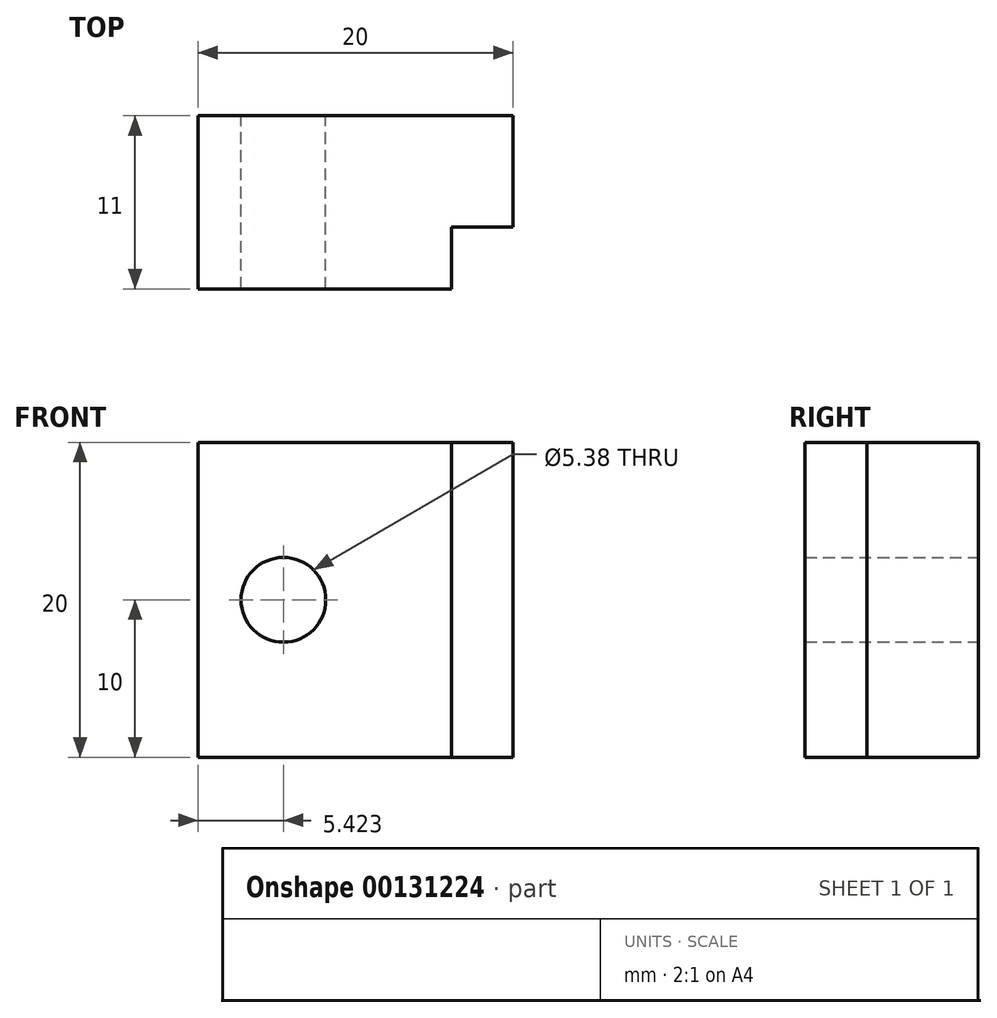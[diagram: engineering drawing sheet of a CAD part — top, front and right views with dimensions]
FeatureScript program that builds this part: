
annotation { "Feature Type Name" : "Feature", "Feature Type Description" : "" }
export const myFeature = defineFeature(function(context is Context, id is Id, definition is map)
    precondition{}
    {
        {
            var Q0;
            Q0=qCreatedBy(makeId("Front.planeOp"),FACE);
            var sketch = newSketch(context, id + "F0", { "sketchPlane" : qUnion([Q0])});
            skLineSegment(sketch, "E0.bottom", {"start": v(0, 0) * mm, "end": v(20, 0) * mm});
            skLineSegment(sketch, "E0.top", {"start": v(0, 20) * mm, "end": v(20, 20) * mm});
            skLineSegment(sketch, "E0.left", {"start": v(0, 0) * mm, "end": v(0, 20) * mm});
            skLineSegment(sketch, "E0.right", {"start": v(20, 0) * mm, "end": v(20, 20) * mm});
            skLineSegment(sketch, "E1", {"start": v(-7.51, 0) * mm, "end": v(-7.51, 10) * mm});
            skLineSegment(sketch, "E2", {"start": v(0, 10) * mm, "end": v(2.7, 10) * mm});
            skPoint(sketch, "E2.endSnap0", {"position": v(0, 10) * mm});
            skCircle(sketch, "E3", {"center": v(5.42, 10) * mm, "radius": 2.7 * mm});
            skSolve(sketch);
        }
        {
            var Q0;
            Q0=makeQuery(id+"F0.imprint","IMPRINT",FACE,{"disambiguationData":[TD([[makeQuery(id+"F0.imprint","IMPRINT",EDGE,{"derivedFrom":sQuery(id+"F0.wireOp",EDGE,"E0.bottom")}),1.0]])]});
            extrude(context, id + "F1", {"entities" : qUnion([Q0]), "depth" : 11 * mm});
        }
        {
            var Q0;
            Q0=qCreatedBy(makeId("Top.planeOp"),FACE);
            var sketch = newSketch(context, id + "F2", { "sketchPlane" : qUnion([Q0])});
            skLineSegment(sketch, "E4", {"start": v(20.56, -11.08) * mm, "end": v(20.56, -7.08) * mm});
            skLineSegment(sketch, "E5", {"start": v(20.09, -11.36) * mm, "end": v(16.09, -11.36) * mm});
            skLineSegment(sketch, "E6", {"start": v(16.09, -11.36) * mm, "end": v(6.09, -11.36) * mm});
            skLineSegment(sketch, "E7", {"start": v(0, 2.37) * mm, "end": v(6, 2.37) * mm});
            skLineSegment(sketch, "E8", {"start": v(6, 1.19) * mm, "end": v(3.3, 1.19) * mm});
            skLineSegment(sketch, "E9", {"start": v(6.09, -12.78) * mm, "end": v(8.79, -12.78) * mm});
            skLineSegment(sketch, "E10.bottom", {"start": v(20.09, -11.08) * mm, "end": v(16.09, -11.08) * mm});
            skLineSegment(sketch, "E10.top", {"start": v(20.09, -7.08) * mm, "end": v(16.09, -7.08) * mm});
            skLineSegment(sketch, "E10.left", {"start": v(20.09, -11.08) * mm, "end": v(20.09, -7.08) * mm});
            skLineSegment(sketch, "E10.right", {"start": v(16.09, -11.08) * mm, "end": v(16.09, -7.08) * mm});
            skLineSegment(sketch, "E11", {"start": v(-3.3, 0) * mm, "end": v(-3.3, -5.5) * mm});
            skSolve(sketch);
        }
        {
            var Q0;
            Q0 = qSketchRegion(id + "F2", true);
            var Q1;
            Q1=makeQuery(id+"F1.opExtrude","SWEPT_FACE",FACE,{"disambiguationData":[OSD([sQuery(id+"F0.wireOp",EDGE,"E0.top")])]});
            extrude(context, id + "F3", {"entities" : qUnion([Q0, Q1]), "operationType" : NewBodyOperationType.REMOVE, "depth" : 25 * mm});
        }
    });
